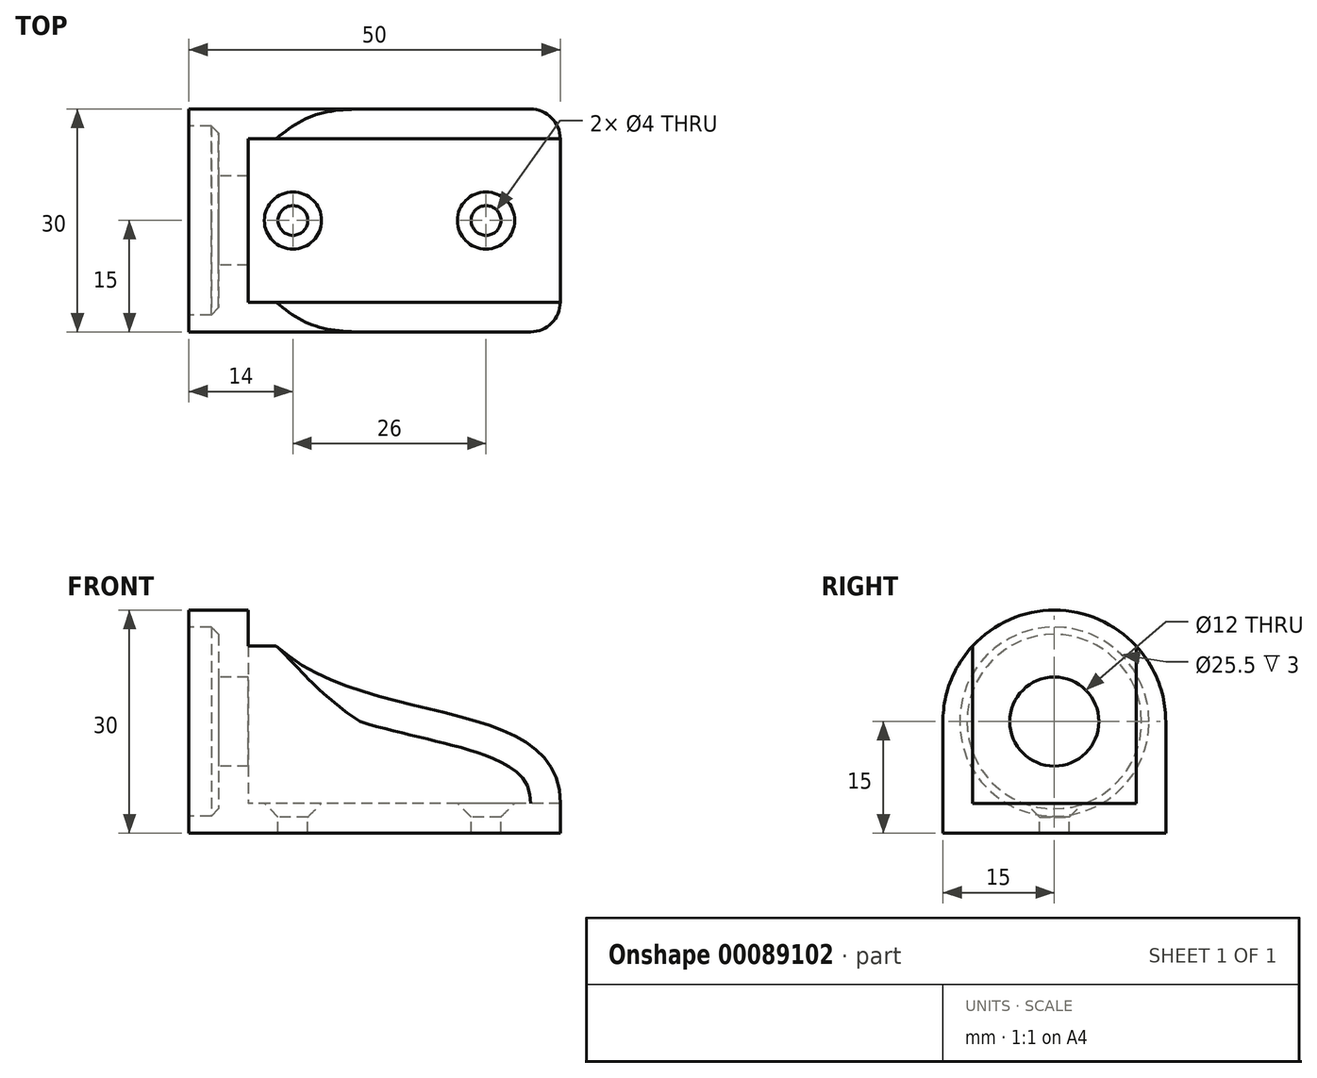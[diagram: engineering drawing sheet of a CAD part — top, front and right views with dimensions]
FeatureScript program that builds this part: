
annotation { "Feature Type Name" : "Feature", "Feature Type Description" : "" }
export const myFeature = defineFeature(function(context is Context, id is Id, definition is map)
    precondition{}
    {
        {
            var Q0;
            Q0=qCreatedBy(makeId("Top.planeOp"),FACE);
            var sketch = newSketch(context, id + "F0", { "sketchPlane" : qUnion([Q0])});
            skLineSegment(sketch, "E0.bottom", {"start": v(25, -15) * mm, "end": v(-25, -15) * mm});
            skLineSegment(sketch, "E0.top", {"start": v(25, 15) * mm, "end": v(-25, 15) * mm});
            skLineSegment(sketch, "E0.left", {"start": v(25, -15) * mm, "end": v(25, 15) * mm});
            skLineSegment(sketch, "E0.right", {"start": v(-25, -15) * mm, "end": v(-25, 15) * mm});
            skPoint(sketch, "E0.middle", {"position": v(0, 0) * mm});
            skLineSegment(sketch, "E1", {"start": v(-17, 15) * mm, "end": v(-17, -15) * mm});
            skSolve(sketch);
        }
        {
            var Q0;
            {var subQ0=sQuery(id+"F0.wireOp",EDGE,"E0.left");Q0=makeQuery(id+"F0.imprint","IMPRINT",FACE,{"disambiguationData":[TD([[makeQuery(id+"F0.imprint","IMPRINT",EDGE,{"derivedFrom":subQ0}),1.0]])]});}
            var Q1;
            {var subQ0=sQuery(id+"F0.wireOp",EDGE,"E0.right");Q1=makeQuery(id+"F0.imprint","IMPRINT",FACE,{"disambiguationData":[TD([[makeQuery(id+"F0.imprint","IMPRINT",EDGE,{"derivedFrom":subQ0}),-1.0]])]});}
            extrude(context, id + "F1", {"entities" : qUnion([Q0, Q1]), "depth" : 4 * mm});
        }
        {
            var Q0;
            Q0=makeQuery(id+"F1.opExtrude","CAP_FACE",FACE,{"disambiguationData":[OSD([sQuery(id+"F0.wireOp",EDGE,"E0.bottom"),sQuery(id+"F0.wireOp",EDGE,"E0.top"),sQuery(id+"F0.wireOp",EDGE,"E0.left"),sQuery(id+"F0.wireOp",EDGE,"E0.right")])],"isStart":false});
            var sketch = newSketch(context, id + "F2", { "sketchPlane" : qUnion([Q0])});
            skLineSegment(sketch, "E2.0", {"start": v(-17, 15) * mm, "end": v(-17, -15) * mm});
            skSolve(sketch);
        }
        {
            var Q0;
            Q0 = qSketchRegion(id + "F2", true);
            var Q1;
            {var subQ0=sQuery(id+"F2.wireOp",EDGE,"E2.0");Q1=makeQuery(id+"F2.imprint","IMPRINT",FACE,{"disambiguationData":[TD([[makeQuery(id+"F2.imprint","IMPRINT",EDGE,{"derivedFrom":subQ0}),-1.0]])]});}
            extrude(context, id + "F3", {"entities" : qUnion([Q0, Q1]), "operationType" : NewBodyOperationType.ADD, "depth" : 26 * mm});
        }
        {
            var Q0;
            {var subQ0=sQuery(id+"F0.wireOp",EDGE,"E0.right");Q0=makeQuery(id+"F3.boolean.opBoolean","MERGE",FACE,{"derivedFrom":[makeQuery(id+"F1.opExtrude","SWEPT_FACE",FACE,{"disambiguationData":[OSD([subQ0])]}),makeQuery(id+"F3.opExtrude","SWEPT_FACE",FACE,{"disambiguationData":[OSD([subQ0])]})]});}
            var sketch = newSketch(context, id + "F4", { "sketchPlane" : qUnion([Q0])});
            skCircle(sketch, "E3", {"center": v(0, 15) * mm, "radius": 6 * mm});
            skPoint(sketch, "E3.centerSnap0", {"position": v(15, 15) * mm});
            skPoint(sketch, "E3.centerSnap1", {"position": v(0, 30) * mm});
            skCircle(sketch, "E4", {"center": v(0, 15) * mm, "radius": 12.75 * mm});
            skSolve(sketch);
        }
        {
            var Q0;
            Q0=makeQuery(id+"F4.imprint","IMPRINT",FACE,{"disambiguationData":[TD([[makeQuery(id+"F4.imprint","IMPRINT",EDGE,{"derivedFrom":sQuery(id+"F4.wireOp",EDGE,"E3")}),1.0]])]});
            extrude(context, id + "F5", {"entities" : qUnion([Q0]), "operationType" : NewBodyOperationType.REMOVE, "endBound" : BoundingType.THROUGH_ALL, "oppositeDirection" : true, "depth" : 25 * mm});
        }
        {
            var Q0;
            Q0=makeQuery(id+"F4.imprint","IMPRINT",FACE,{"disambiguationData":[TD([[makeQuery(id+"F4.imprint","IMPRINT",EDGE,{"derivedFrom":sQuery(id+"F4.wireOp",EDGE,"E3")}),-1.0]])]});
            extrude(context, id + "F6", {"entities" : qUnion([Q0]), "operationType" : NewBodyOperationType.REMOVE, "oppositeDirection" : true, "depth" : 4 * mm});
        }
        {
            var Q0;
            Q0=makeQuery(id+"F6.boolean.opBoolean","COPY",EDGE,{"derivedFrom":makeQuery(id+"F6.opExtrude","CAP_EDGE",EDGE,{"disambiguationData":[OSD([sQuery(id+"F4.wireOp",EDGE,"E4")])],"isStart":false})});
            chamfer(context, id + "F7", {"entities" : qUnion([Q0]), "width" : 1 * mm, "tangentPropagation" : true});
        }
        {
            var Q0;
            Q0=makeQuery(id+"F1.opExtrude","CAP_FACE",FACE,{"disambiguationData":[OSD([sQuery(id+"F0.wireOp",EDGE,"E0.bottom"),sQuery(id+"F0.wireOp",EDGE,"E0.top"),sQuery(id+"F0.wireOp",EDGE,"E0.left"),sQuery(id+"F0.wireOp",EDGE,"E0.right")])],"isStart":false});
            var sketch = newSketch(context, id + "F8", { "sketchPlane" : qUnion([Q0])});
            skLineSegment(sketch, "E5", {"start": v(-17, 0) * mm, "end": v(25, 0) * mm, "construction": true});
            skPoint(sketch, "E6", {"position": v(-11, 0) * mm});
            skPoint(sketch, "E7", {"position": v(15, 0) * mm});
            skSolve(sketch);
        }
        {
            var Q0;
            Q0=sQuery(id+"F8.wireOp",VERTEX,"E6");
            var Q1;
            Q1=sQuery(id+"F8.wireOp",VERTEX,"E7");
            var Q2;
            Q2=makeQuery(id+"F1.opExtrude","SWEPT_BODY",BODY,{"disambiguationData":[OSD([sQuery(id+"F0.wireOp",EDGE,"E0.bottom"),sQuery(id+"F0.wireOp",EDGE,"E0.top"),sQuery(id+"F0.wireOp",EDGE,"E0.left"),sQuery(id+"F0.wireOp",EDGE,"E0.right")])]});
            hole(context, id + "F9", {"style" : HoleStyle.C_SINK, "endStyle" : HoleEndStyle.THROUGH, "holeDiameter" : 4 * mm, "cSinkDiameter" : 7.7 * mm, "cSinkAngle" : 90 * degree, "locations" : qUnion([Q0, Q1]), "scope" : qUnion([Q2]), "isTappedThrough" : true});
        }
        {
            var Q0;
            {var subQ0=sQuery(id+"F0.wireOp",EDGE,"E0.bottom");Q0=makeQuery(id+"F3.boolean.opBoolean","MERGE",FACE,{"derivedFrom":[makeQuery(id+"F1.opExtrude","SWEPT_FACE",FACE,{"disambiguationData":[OSD([subQ0])]}),makeQuery(id+"F3.opExtrude","SWEPT_FACE",FACE,{"disambiguationData":[OSD([subQ0])]})]});}
            var sketch = newSketch(context, id + "F10", { "sketchPlane" : qUnion([Q0])});
            skFitSpline(sketch, "E8", {"points": [v(-17, 30) * mm, v(25, 4) * mm], "startDerivative": vector(28.05, -52.4) * mm, "endDerivative": vector(0, -49.8) * mm});
            skSolve(sketch);
        }
        {
            var Q0;
            Q0=makeQuery(id+"F10.imprint","IMPRINT",FACE,{"disambiguationData":[TD([[makeQuery(id+"F10.imprint","IMPRINT",EDGE,{"derivedFrom":sQuery(id+"F10.wireOp",EDGE,"E8")}),-1.0]])]});
            extrude(context, id + "F11", {"entities" : qUnion([Q0]), "oppositeDirection" : true, "depth" : 4 * mm});
        }
        {
            var Q0;
            Q0=makeQuery(id+"F1.opExtrude","SWEPT_EDGE",EDGE,{"disambiguationData":[OSD([sQuery(id+"F0.wireOp",EDGE,"E0.bottom"),sQuery(id+"F0.wireOp",EDGE,"E0.left")])]});
            var Q1;
            Q1=makeQuery(id+"F11.opExtrude","CAP_EDGE",EDGE,{"disambiguationData":[OSD([sQuery(id+"F10.wireOp",EDGE,"E8")])],"isStart":true});
            var Q2;
            Q2=makeQuery(id+"F14.opFillet","BLEND_EDGE",EDGE,{"blendedFrom":[makeQuery(id+"F3.opExtrude","CAP_EDGE",EDGE,{"disambiguationData":[OSD([sQuery(id+"F0.wireOp",EDGE,"E0.bottom")])],"isStart":false}),makeQuery(id+"F11.opExtrude","SWEPT_FACE",FACE,{"disambiguationData":[OSD([sQuery(id+"F10.wireOp",EDGE,"E8")])]})],"blendedInto":[makeQuery(id+"F11.opExtrude","SWEPT_FACE",FACE,{"disambiguationData":[OSD([sQuery(id+"F10.wireOp",EDGE,"E8")])]})]});
            var Q3;
            {var subQ0=sQuery(id+"F0.wireOp",EDGE,"E0.bottom");Q3=makeQuery(id+"F14.opFillet","BLEND_EDGE",EDGE,{"blendedFrom":[makeQuery(id+"F3.opExtrude","CAP_EDGE",EDGE,{"disambiguationData":[OSD([subQ0])],"isStart":false}),makeQuery(id+"F11.opExtrude","CAP_FACE",FACE,{"disambiguationData":[OSD([subQ0,sQuery(id+"F2.wireOp",EDGE,"E2.0"),sQuery(id+"F10.wireOp",EDGE,"E8")])],"isStart":false})],"blendedInto":[makeQuery(id+"F11.opExtrude","CAP_FACE",FACE,{"disambiguationData":[OSD([subQ0,sQuery(id+"F2.wireOp",EDGE,"E2.0"),sQuery(id+"F10.wireOp",EDGE,"E8")])],"isStart":false})]});}
            var Q4;
            Q4=makeQuery(id+"F1.opExtrude","SWEPT_EDGE",EDGE,{"disambiguationData":[OSD([sQuery(id+"F0.wireOp",EDGE,"E0.top"),sQuery(id+"F0.wireOp",EDGE,"E0.left")])]});
            fillet(context, id + "F12", {"entities" : qUnion([Q0, Q1, Q2, Q3, Q4]), "radius" : 4 * mm, "tangentPropagation" : true, "allowEdgeOverflow" : false});
        }
        {
            var Q0;
            Q0=makeQuery(id+"F11.opExtrude","SWEPT_BODY",BODY,{"disambiguationData":[OSD([sQuery(id+"F0.wireOp",EDGE,"E0.bottom"),sQuery(id+"F2.wireOp",EDGE,"E2.0"),sQuery(id+"F10.wireOp",EDGE,"qezYiWbJ-CwZR-qfbR-ZVjk-myLgsKKm8BRc"),sQuery(id+"F10.wireOp",EDGE,"kQqjfgwl-odIY-JrLN-5yaW-krHz6nRqVGTw")])]});
            var Q1;
            Q1=qCreatedBy(makeId("Front.planeOp"),FACE);
            mirror(context, id + "F13", {"operationType" : NewBodyOperationType.ADD, "entities" : qUnion([Q0]), "mirrorPlane" : qUnion([Q1])});
        }
        {
            var Q0;
            Q0=makeQuery(id+"F3.opExtrude","CAP_EDGE",EDGE,{"disambiguationData":[OSD([sQuery(id+"F0.wireOp",EDGE,"E0.bottom")])],"isStart":false});
            var Q1;
            Q1=makeQuery(id+"F3.opExtrude","CAP_EDGE",EDGE,{"disambiguationData":[OSD([sQuery(id+"F0.wireOp",EDGE,"E0.top")])],"isStart":false});
            fillet(context, id + "F14", {"entities" : qUnion([Q0, Q1]), "radius" : 15 * mm, "tangentPropagation" : true, "allowEdgeOverflow" : false});
        }
    });
